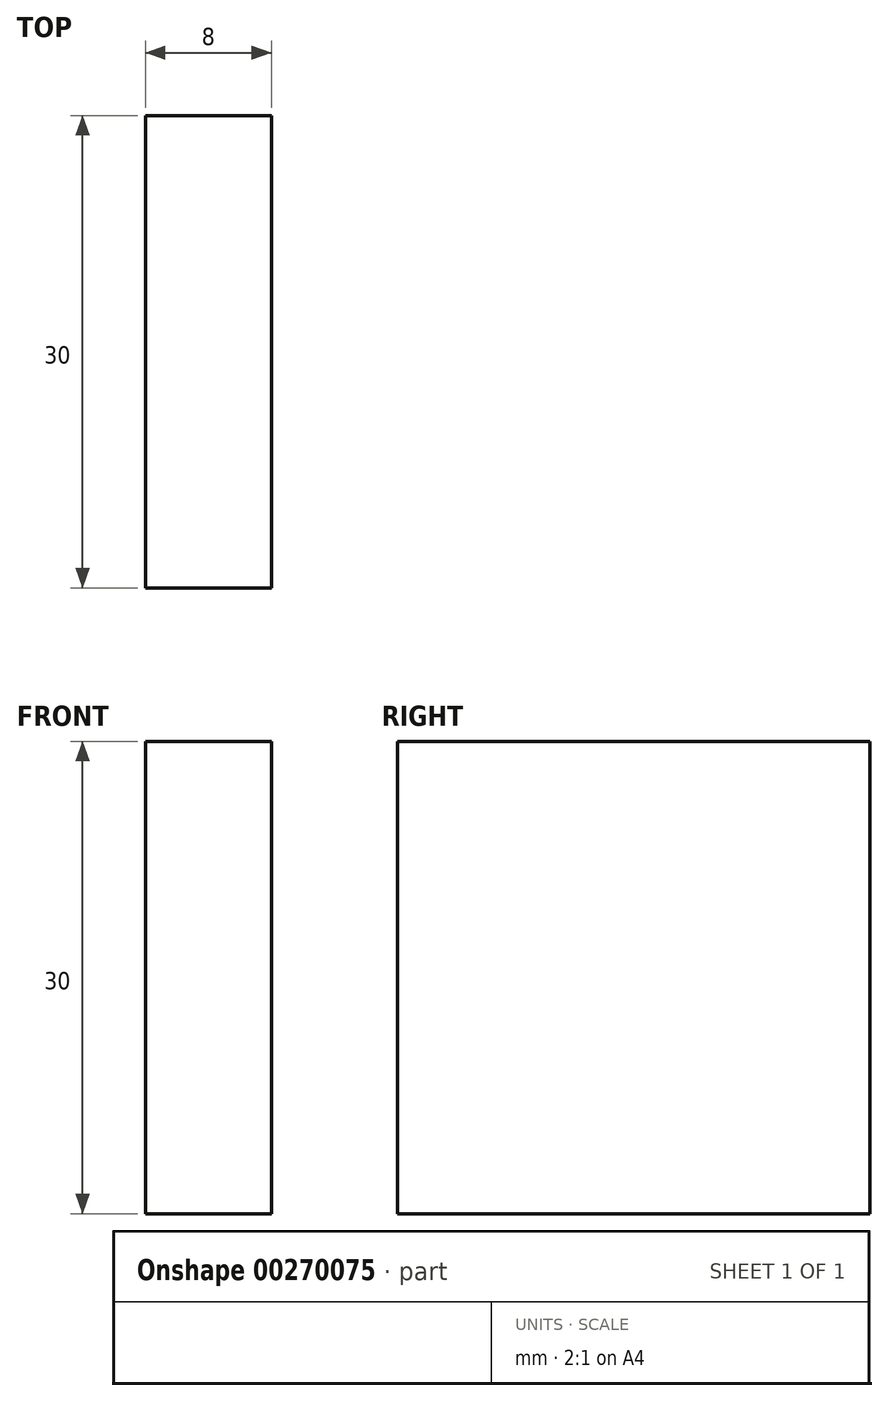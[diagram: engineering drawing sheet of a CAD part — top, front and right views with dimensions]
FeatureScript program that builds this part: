
annotation { "Feature Type Name" : "Feature", "Feature Type Description" : "" }
export const myFeature = defineFeature(function(context is Context, id is Id, definition is map)
    precondition{}
    {
        {
            var Q0;
            Q0=qCreatedBy(makeId("Right.planeOp"),FACE);
            var sketch = newSketch(context, id + "F0", { "sketchPlane" : qUnion([Q0])});
            skLineSegment(sketch, "E0.bottom", {"start": v(10.04, 10.46) * mm, "end": v(-19.96, 10.46) * mm});
            skLineSegment(sketch, "E0.top", {"start": v(10.04, -19.54) * mm, "end": v(-19.96, -19.54) * mm});
            skLineSegment(sketch, "E0.left", {"start": v(10.04, 10.46) * mm, "end": v(10.04, -19.54) * mm});
            skLineSegment(sketch, "E0.right", {"start": v(-19.96, 10.46) * mm, "end": v(-19.96, -19.54) * mm});
            skPoint(sketch, "E0.middle", {"position": v(-4.96, -4.54) * mm});
            skSolve(sketch);
        }
        {
            var Q0;
            Q0=makeQuery(id+"F0.imprint","IMPRINT",FACE,{"disambiguationData":[TD([[makeQuery(id+"F0.imprint","IMPRINT",EDGE,{"derivedFrom":sQuery(id+"F0.wireOp",EDGE,"E0.bottom")}),1.0]])]});
            extrude(context, id + "F1", {"entities" : qUnion([Q0]), "depth" : 8 * mm});
        }
    });
